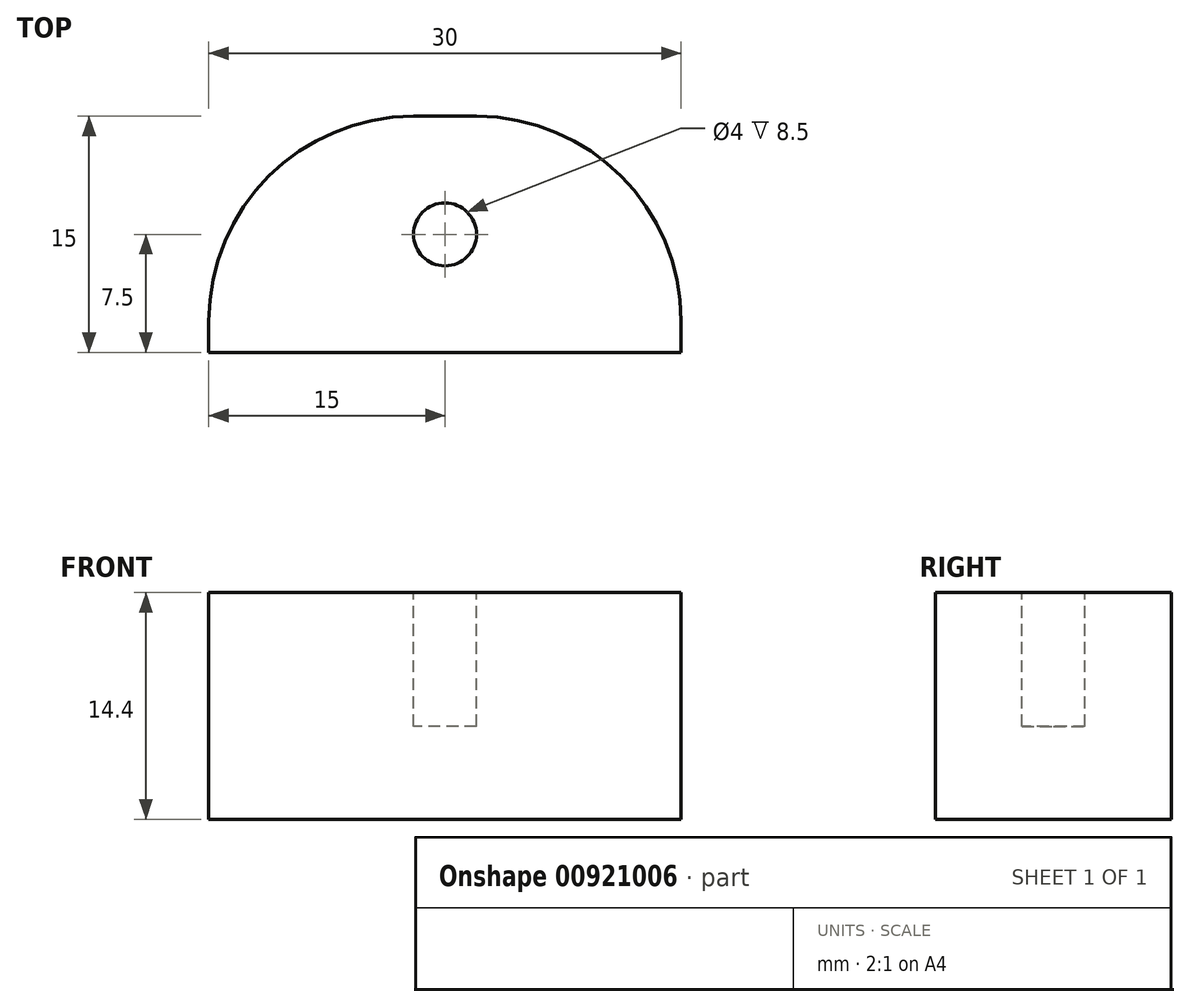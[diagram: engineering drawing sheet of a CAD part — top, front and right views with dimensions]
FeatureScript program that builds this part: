
annotation { "Feature Type Name" : "Feature", "Feature Type Description" : "" }
export const myFeature = defineFeature(function(context is Context, id is Id, definition is map)
    precondition{}
    {
        {
            var Q0;
            Q0=qCreatedBy(makeId("Right.planeOp"),FACE);
            var sketch = newSketch(context, id + "F0", { "sketchPlane" : qUnion([Q0])});
            skLineSegment(sketch, "E0.bottom", {"start": v(15, 1.57) * mm, "end": v(0, 1.57) * mm});
            skLineSegment(sketch, "E0.top", {"start": v(15, 15.97) * mm, "end": v(0, 15.97) * mm});
            skLineSegment(sketch, "E0.left", {"start": v(15, 1.57) * mm, "end": v(15, 15.97) * mm});
            skLineSegment(sketch, "E0.right", {"start": v(0, 1.57) * mm, "end": v(0, 15.97) * mm});
            skSolve(sketch);
        }
        {
            var Q0;
            Q0=makeQuery(id+"F0.imprint","IMPRINT",FACE,{"disambiguationData":[TD([[makeQuery(id+"F0.imprint","IMPRINT",EDGE,{"derivedFrom":sQuery(id+"F0.wireOp",EDGE,"E0.bottom")}),-1.0]])]});
            extrude(context, id + "F1", {"entities" : qUnion([Q0]), "endBound" : BoundingType.SYMMETRIC, "depth" : 30 * mm, "offsetDistance" : 25 * mm});
        }
        {
            var Q0;
            Q0=makeQuery(id+"F1.opExtrude","CAP_EDGE",EDGE,{"disambiguationData":[OSD([sQuery(id+"F0.wireOp",EDGE,"E0.left")])],"isStart":true});
            var Q1;
            Q1=makeQuery(id+"F1.opExtrude","CAP_EDGE",EDGE,{"disambiguationData":[OSD([sQuery(id+"F0.wireOp",EDGE,"E0.left")])],"isStart":false});
            fillet(context, id + "F2", {"entities" : qUnion([Q0, Q1]), "radius" : 13 * mm, "tangentPropagation" : true, "allowEdgeOverflow" : false});
        }
        {
            var Q0;
            Q0=makeQuery(id+"F1.opExtrude","SWEPT_FACE",FACE,{"disambiguationData":[OSD([sQuery(id+"F0.wireOp",EDGE,"E0.top")])]});
            var sketch = newSketch(context, id + "F3", { "sketchPlane" : qUnion([Q0])});
            skCircle(sketch, "E1", {"center": v(0, 7.5) * mm, "radius": 2 * mm});
            skSolve(sketch);
        }
        {
            var Q0;
            Q0=makeQuery(id+"F3.imprint","IMPRINT",FACE,{"disambiguationData":[TD([[makeQuery(id+"F3.imprint","IMPRINT",EDGE,{"derivedFrom":sQuery(id+"F3.wireOp",EDGE,"E1")}),1.0]])]});
            extrude(context, id + "F4", {"entities" : qUnion([Q0]), "operationType" : NewBodyOperationType.REMOVE, "oppositeDirection" : true, "depth" : 8.5 * mm, "offsetDistance" : 25 * mm});
        }
    });
